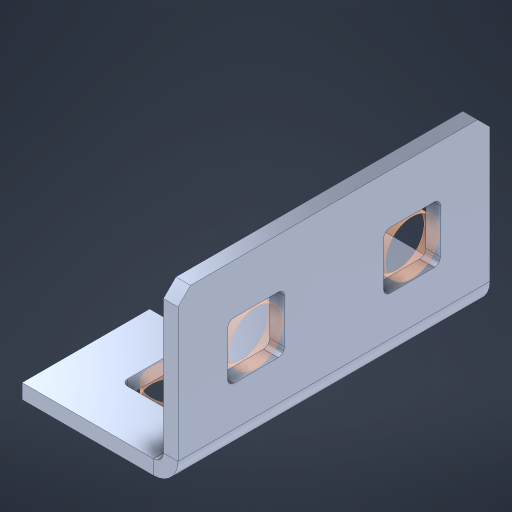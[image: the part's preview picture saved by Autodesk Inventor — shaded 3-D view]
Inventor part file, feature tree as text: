
AUTODESK INVENTOR PART (.ipt)
format: ipt  version: 2023 (Build 270158000, 158)  size: 503,808 bytes
history: native  units: in
note: dims shown in document units (in); Inventor stores cm internally (conversion verified against a paired STEP export)
features: other x13, sheet_metal_op x11, sketch x10, extrude x4, pattern_linear x2, mirror x1, chamfer x1
ambient origin geometry x8: Origin, YZ Plane, XZ Plane, XY Plane, X Axis, Y Axis, Z Axis, Center Point
bodies: Solid1 (feature_tree), Body (feature_tree)
feature tree (42):
  sheet_metal_op  "Flanges"
  other  "Flange Pattern Plane"
  other  "Flange Pattern Sketch"
  sheet_metal_op  "Flange Pattern"
  sheet_metal_op  "Body Pattern"
  pattern_linear  "Center Pattern"  Spacing1=0.0469in  [1 undecoded]
  other  "Arc Length"
  mirror  "Notch Mirror"
  pattern_linear  "Notch Pattern"  Spacing1=0.182in  [1 undecoded]
  chamfer  "End Chamfer"
  extrude  "Half Cut"  Depth=0.02in
  sketch  "Sketch1"  dims[d0=1.0in]
  other  "Plate1"
  sketch  "Sketch2"  dims[d1=1.0in]
  other  "Plate2"
  sheet_metal_op  "Bend1"
  sheet_metal_op  "Corner1"
  sketch  "Sketch3"  dims[d2=0.0469in]
  sketch  "Sketch7"  dims[d3=0.0469in]
  other  "Srf1"
  other  "Srf2"
  sketch  "Sketch8"  dims[d4=0.0234in]
  sketch  "Sketch9"  dims[d5=0.0938in]
  other  "Srf91"
  sheet_metal_op  "Body Pattern Sketch"
  other  "Srf92"
  sketch  "Sketch13"  dims[d6=0.0469in]
  sketch  "Sketch14"  dims[d7=0.5in d8=90.0deg d9=0.0312in]
  sketch  "Sketch15"  dims[d10=0.1875in]
  sketch  "Sketch16"  dims[d11=0.0469in d12=0.0469in d16=0.182in d17=0.02in d18=0.0469in d19=0.0in d20=0.25in d21=0.25in d38=0.7874in d40=0.5in d41=0.3937in d43=1.0in d46=0.172in d47=1.0in d48=0.0in d49=0.182in d50=0.02in d51=0.25in d52=0.25in d53=0.0469in d54=0.0in d55=0.172in d56=1.0in d57=0.0in d58=0.25in d60=0.7874in d62=0.5in d63=0.3937in d65=0.5in d85=0.1227in d86=0.1659in d88=0.04in d89=0.0469in d90=0.0in d91=0.04in d92=0.0491in d95=2.5in d96=0.04in d97=0.25in d98=45.0deg d99=0.25in d100=0.5in d101=0.0in d102=2.497in d106=0.182in d107=0.02in d108=0.5in d109=0.5in d110=0.0469in d111=0.0in d112=0.172in d113=0.5in d114=0.0in d117=0.5in d118=0.5in d119=0.5in]
  other  "Srf786"
  other  "Srf889"
  sheet_metal_op  "Flange Stamp"
  sheet_metal_op  "Flange Circle"
  sheet_metal_op  "Body Stamp"
  sheet_metal_op  "Body Circle"
  other  "Center Stamp"
  other  "Center Circle"
  sheet_metal_op  "Notch"
  extrude  "ExtrusionSrf2"  Depth=0.0469in
  extrude  "ExtrusionSrf92"  TaperAngle=0.0deg  [1 undecoded]
  extrude  "ExtrusionSrf889"  Depth=0.25in
note: 3 required parameter values undecoded (feature->parameter linkage not recoverable at this tier; creation-order binding heuristic only, values carry confidence <= 0.55)
